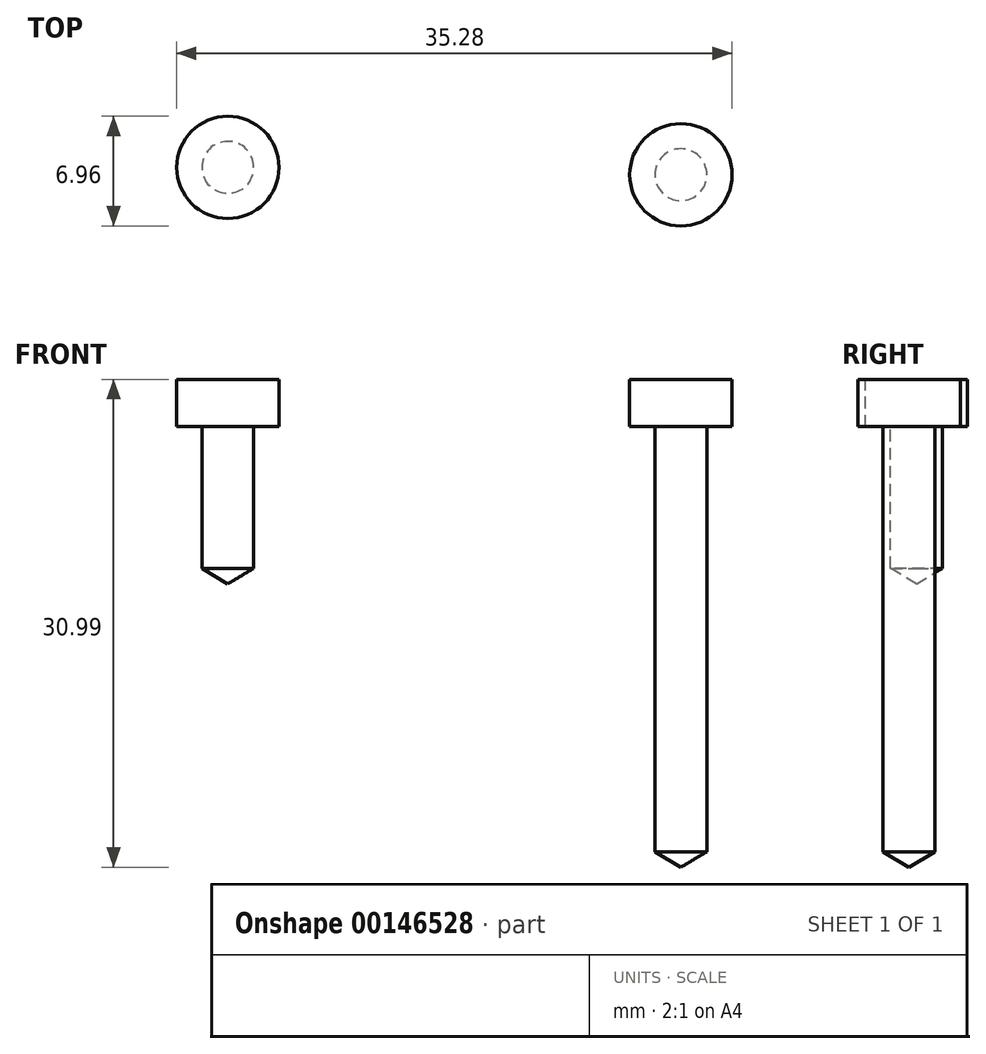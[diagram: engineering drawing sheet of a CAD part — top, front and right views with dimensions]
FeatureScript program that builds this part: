
annotation { "Feature Type Name" : "Feature", "Feature Type Description" : "" }
export const myFeature = defineFeature(function(context is Context, id is Id, definition is map)
    precondition{}
    {
        {
            var Q0;
            Q0=qCreatedBy(makeId("Top.planeOp"),FACE);
            var sketch = newSketch(context, id + "F0", { "sketchPlane" : qUnion([Q0])});
            skLineSegment(sketch, "E0.bottom", {"start": v(29.71, -29) * mm, "end": v(-29.71, -29) * mm});
            skLineSegment(sketch, "E0.top", {"start": v(29.71, 29) * mm, "end": v(-29.71, 29) * mm});
            skLineSegment(sketch, "E0.left", {"start": v(29.71, -29) * mm, "end": v(29.71, 29) * mm});
            skLineSegment(sketch, "E0.right", {"start": v(-29.71, -29) * mm, "end": v(-29.71, 29) * mm});
            skPoint(sketch, "E0.middle", {"position": v(0, 0) * mm});
            skPoint(sketch, "E1", {"position": v(-14.04, 13.8) * mm});
            skPoint(sketch, "E2", {"position": v(14.74, 13.34) * mm});
            skSolve(sketch);
        }
        {
            var Q0;
            Q0=makeQuery(id+"F0.imprint","IMPRINT",FACE,{"disambiguationData":[TD([[makeQuery(id+"F0.imprint","IMPRINT",EDGE,{"derivedFrom":sQuery(id+"F0.wireOp",EDGE,"E0.bottom")}),-1.0]])]});
            extrude(context, id + "F1", {"entities" : qUnion([Q0]), "oppositeDirection" : true, "depth" : 79 * mm});
        }
        {
            var Q0;
            Q0=sQuery(id+"F0.wireOp",VERTEX,"E1");
            var Q1;
            Q1=makeQuery(id+"F1.opExtrude","SWEPT_BODY",BODY,{"disambiguationData":[OSD([sQuery(id+"F0.wireOp",EDGE,"E0.bottom"),sQuery(id+"F0.wireOp",EDGE,"E0.top"),sQuery(id+"F0.wireOp",EDGE,"E0.left"),sQuery(id+"F0.wireOp",EDGE,"E0.right")])]});
            hole(context, id + "F2", {"style" : HoleStyle.C_BORE, "endStyle" : HoleEndStyle.BLIND, "standardTappedOrClearance" : lookupTablePath({ "standard" : "ISO", "fit" : "Normal", "size" : "M3", "type" : "Clearance" }), "standardBlindInLast" : lookupTablePath({ "fit" : "Standard", "standard" : "ISO", "size" : "M3", "type" : "Clearance" }), "holeDiameter" : 3.3 * mm, "cBoreDiameter" : 6.5 * mm, "cBoreDepth" : 3 * mm, "holeDepth" : 12 * mm, "startFromSketch" : true, "locations" : qUnion([Q0]), "scope" : qUnion([Q1])});
        }
        {
            var Q0;
            Q0=sQuery(id+"F0.wireOp",VERTEX,"E2");
            var Q1;
            Q1=makeQuery(id+"F1.opExtrude","SWEPT_BODY",BODY,{"disambiguationData":[OSD([sQuery(id+"F0.wireOp",EDGE,"E0.bottom"),sQuery(id+"F0.wireOp",EDGE,"E0.top"),sQuery(id+"F0.wireOp",EDGE,"E0.left"),sQuery(id+"F0.wireOp",EDGE,"E0.right")])]});
            hole(context, id + "F3", {"style" : HoleStyle.C_BORE, "endStyle" : HoleEndStyle.BLIND, "standardTappedOrClearance" : lookupTablePath({ "standard" : "ISO", "fit" : "Normal", "size" : "M3", "type" : "Clearance" }), "standardBlindInLast" : lookupTablePath({ "fit" : "Standard", "standard" : "ISO", "size" : "M3", "type" : "Clearance" }), "holeDiameter" : 3.3 * mm, "cBoreDiameter" : 6.5 * mm, "cBoreDepth" : 3 * mm, "holeDepth" : 30 * mm, "startFromSketch" : true, "locations" : qUnion([Q0]), "scope" : qUnion([Q1])});
        }
        {
            var Q0;
            Q0=makeQuery(id+"F1.opExtrude","CAP_FACE",FACE,{"disambiguationData":[OSD([sQuery(id+"F0.wireOp",EDGE,"E0.bottom"),sQuery(id+"F0.wireOp",EDGE,"E0.top"),sQuery(id+"F0.wireOp",EDGE,"E0.left"),sQuery(id+"F0.wireOp",EDGE,"E0.right")])],"isStart":false});
            var Q1;
            Q1=makeQuery(id+"F1.opExtrude","CAP_FACE",FACE,{"disambiguationData":[OSD([sQuery(id+"F0.wireOp",EDGE,"E0.bottom"),sQuery(id+"F0.wireOp",EDGE,"E0.top"),sQuery(id+"F0.wireOp",EDGE,"E0.left"),sQuery(id+"F0.wireOp",EDGE,"E0.right")])],"isStart":true});
            extrude(context, id + "F4", {"entities" : qUnion([Q0]), "endBound" : BoundingType.UP_TO_SURFACE, "oppositeDirection" : true, "endBoundEntityFace" : qUnion([Q1]), "depth" : 25.4 * mm});
        }
        {
            var Q0;
            Q0=makeQuery(id+"F1.opExtrude","SWEPT_BODY",BODY,{"disambiguationData":[OSD([sQuery(id+"F0.wireOp",EDGE,"E0.bottom"),sQuery(id+"F0.wireOp",EDGE,"E0.top"),sQuery(id+"F0.wireOp",EDGE,"E0.left"),sQuery(id+"F0.wireOp",EDGE,"E0.right")])]});
            var Q1;
            Q1=makeQuery(id+"F4.opExtrude","SWEPT_BODY",BODY,{"disambiguationData":[OSD([sQuery(id+"F0.wireOp",EDGE,"E0.bottom"),sQuery(id+"F0.wireOp",EDGE,"E0.top"),sQuery(id+"F0.wireOp",EDGE,"E0.left"),sQuery(id+"F0.wireOp",EDGE,"E0.right")])]});
            booleanBodies(context, id + "F5", {"operationType" : BooleanOperationType.SUBTRACTION, "tools" : qUnion([Q0]), "targets" : qUnion([Q1])});
        }
    });
